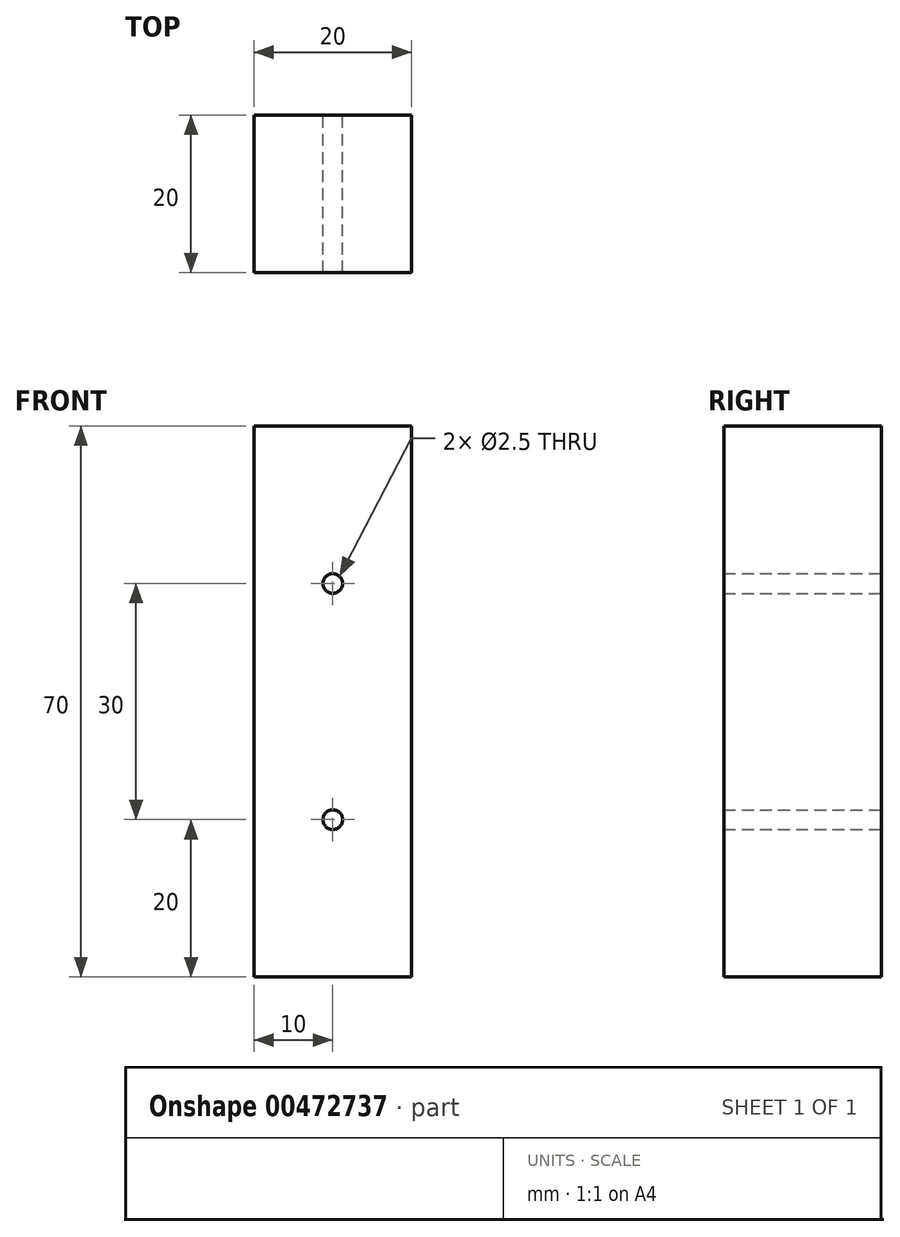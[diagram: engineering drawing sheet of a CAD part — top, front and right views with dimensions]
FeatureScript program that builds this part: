
annotation { "Feature Type Name" : "Feature", "Feature Type Description" : "" }
export const myFeature = defineFeature(function(context is Context, id is Id, definition is map)
    precondition{}
    {
        {
            var Q0;
            Q0=qCreatedBy(makeId("Front.planeOp"),FACE);
            var sketch = newSketch(context, id + "F0", { "sketchPlane" : qUnion([Q0])});
            skLineSegment(sketch, "E0.bottom", {"start": v(0, 0) * mm, "end": v(20, 0) * mm});
            skLineSegment(sketch, "E0.top", {"start": v(0, -70) * mm, "end": v(20, -70) * mm});
            skLineSegment(sketch, "E0.left", {"start": v(0, 0) * mm, "end": v(0, -70) * mm});
            skLineSegment(sketch, "E0.right", {"start": v(20, 0) * mm, "end": v(20, -70) * mm});
            skLineSegment(sketch, "E1", {"start": v(10, 0) * mm, "end": v(10, -70) * mm, "construction": true});
            skLineSegment(sketch, "E2", {"start": v(20, -50) * mm, "end": v(0, -50) * mm, "construction": true});
            skLineSegment(sketch, "E3", {"start": v(20, -20) * mm, "end": v(0, -20) * mm, "construction": true});
            skCircle(sketch, "E4", {"center": v(10, -20) * mm, "radius": 1.25 * mm});
            skCircle(sketch, "E5", {"center": v(10, -50) * mm, "radius": 1.25 * mm});
            skSolve(sketch);
        }
        {
            var Q0;
            Q0 = qSketchRegion(id + "F0", true);
            extrude(context, id + "F1", {"entities" : qUnion([Q0]), "depth" : 20 * mm});
        }
    });
